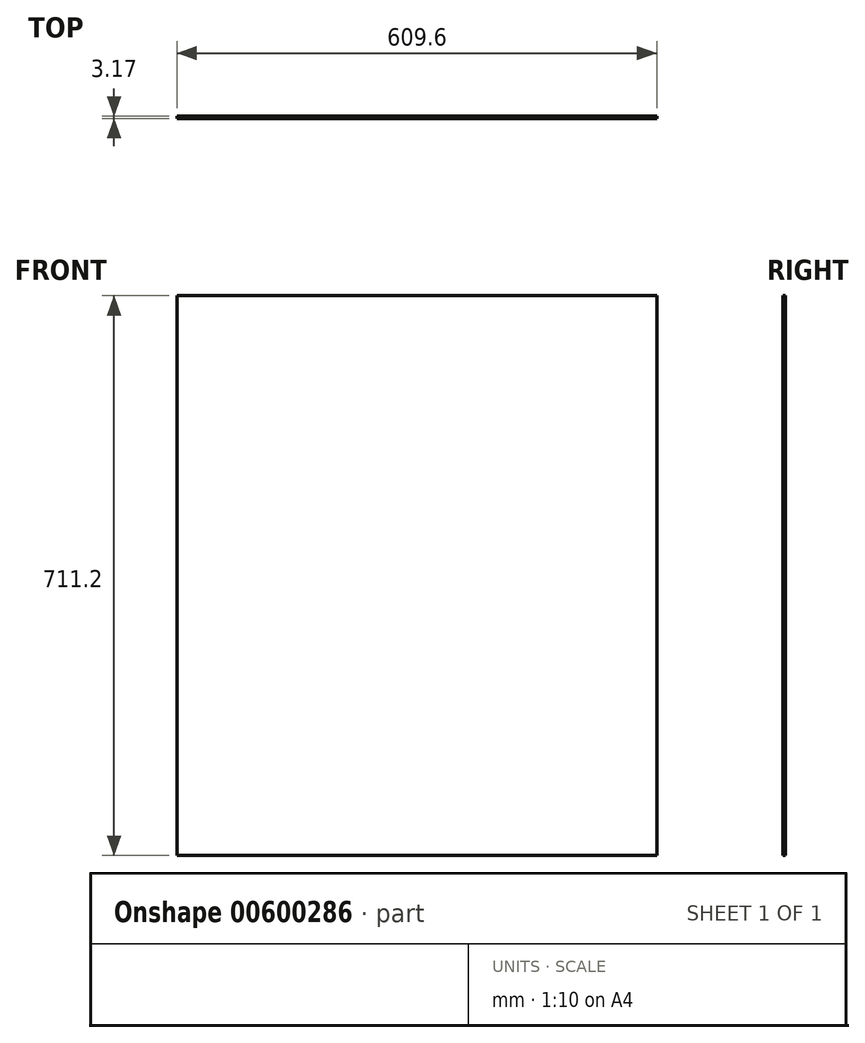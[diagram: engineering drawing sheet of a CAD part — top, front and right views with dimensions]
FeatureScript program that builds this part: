
annotation { "Feature Type Name" : "Feature", "Feature Type Description" : "" }
export const myFeature = defineFeature(function(context is Context, id is Id, definition is map)
    precondition{}
    {
        {
            var Q0;
            Q0=qCreatedBy(makeId("Front.planeOp"),FACE);
            var sketch = newSketch(context, id + "F0", { "sketchPlane" : qUnion([Q0])});
            skLineSegment(sketch, "E0.bottom", {"start": v(304.8, 355.6) * mm, "end": v(-304.8, 355.6) * mm});
            skLineSegment(sketch, "E0.top", {"start": v(304.8, -355.6) * mm, "end": v(-304.8, -355.6) * mm});
            skLineSegment(sketch, "E0.left", {"start": v(304.8, 355.6) * mm, "end": v(304.8, -355.6) * mm});
            skLineSegment(sketch, "E0.right", {"start": v(-304.8, 355.6) * mm, "end": v(-304.8, -355.6) * mm});
            skPoint(sketch, "E0.middle", {"position": v(0, 0) * mm});
            skSolve(sketch);
        }
        {
            var Q0;
            Q0 = qSketchRegion(id + "F0", true);
            extrude(context, id + "F1", {"entities" : qUnion([Q0]), "oppositeDirection" : true, "depth" : 3.17 * mm, "offsetDistance" : 25.4 * mm});
        }
    });
